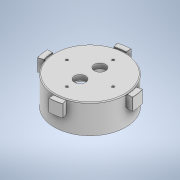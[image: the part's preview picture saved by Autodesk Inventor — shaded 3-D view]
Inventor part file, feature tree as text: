
AUTODESK INVENTOR PART (.ipt)
format: ipt  version: 2020 (Build 240168000, 168)  size: 638,464 bytes
history: native  units: mm
features: fillet x12, sketch x6, extrude x4, hole x2
ambient origin geometry x8: Origin, YZ Plane, XZ Plane, XY Plane, X Axis, Y Axis, Z Axis, Center Point
bodies: Solid1 (feature_tree)
feature tree (24):
  extrude  "Extrusion1"  Depth=57.0mm
  extrude  "Extrusion2"  Depth=58.4mm
  extrude  "Extrusion3"  Depth=15.58579mm
  extrude  "Extrusion4"  Depth=31.293753mm
  hole  "Hole1"  [1 undecoded]
  hole  "Hole2"  [1 undecoded]
  fillet  "Fillet1"  Radius=3.106686mm
  fillet  "Fillet2"  Radius=4.0mm
  fillet  "Fillet3"  Radius=58.4mm
  fillet  "Fillet4"  Radius=57.0mm
  fillet  "Fillet5"  Radius=12.849114mm
  fillet  "Fillet6"  Radius=28.557077mm
  fillet  "Fillet10"  Radius=18.566813mm
  fillet  "Fillet12"  Radius=2.858849mm
  fillet  "Fillet13"  Radius=3.3mm
  fillet  "Fillet14"  Radius=57.0mm
  fillet  "Fillet15"  Radius=4.0mm
  fillet  "Fillet16"  Radius=15.9mm
  sketch  "Sketch1"  dims[d0=48.5mm d1=57.0mm]
  sketch  "Sketch2"  dims[d2=19.0mm d3=0.0mm d4=58.4mm]
  sketch  "Sketch3"  dims[d5=67.0mm d6=15.58579mm]
  sketch  "Sketch4"  dims[d7=12.601277mm d8=31.293753mm]
  sketch  "Sketch5"  dims[d9=28.30924mm d10=15.830136mm]
  sketch  "Sketch6"  dims[d11=18.814649mm d12=0.122173mm d13=3.106686mm d14=4.0mm d15=6.0mm d16=0.0mm d17=0.0mm d18=58.4mm d19=57.0mm d20=12.849114mm d21=28.557077mm d22=18.566813mm d23=2.858849mm d24=3.3mm d25=5.3mm d26=0.0mm d27=0.0mm d28=57.0mm d29=4.0mm d30=0.0mm d31=15.9mm d32=8.7mm d33=8.7mm d34=9.0mm d35=6.0mm d36=4.0mm d37=2.0mm d38=90.0deg d39=8.0mm d40=20.594885mm d41=36.9mm d42=0.7mm d43=0.7mm d44=0.7mm d45=0.7mm d46=1.5mm d47=6.0mm d48=4.0mm d49=2.0mm d50=90.0deg d51=8.0mm d52=20.594885mm d53=0.7mm d54=0.2mm d55=0.7mm d56=0.1mm d57=0.2mm d58=0.2mm d62=0.2mm d64=0.2mm d65=0.2mm d66=0.2mm d67=0.2mm d68=0.2mm]
note: 2 required parameter values undecoded (feature->parameter linkage not recoverable at this tier; creation-order binding heuristic only, values carry confidence <= 0.55)
